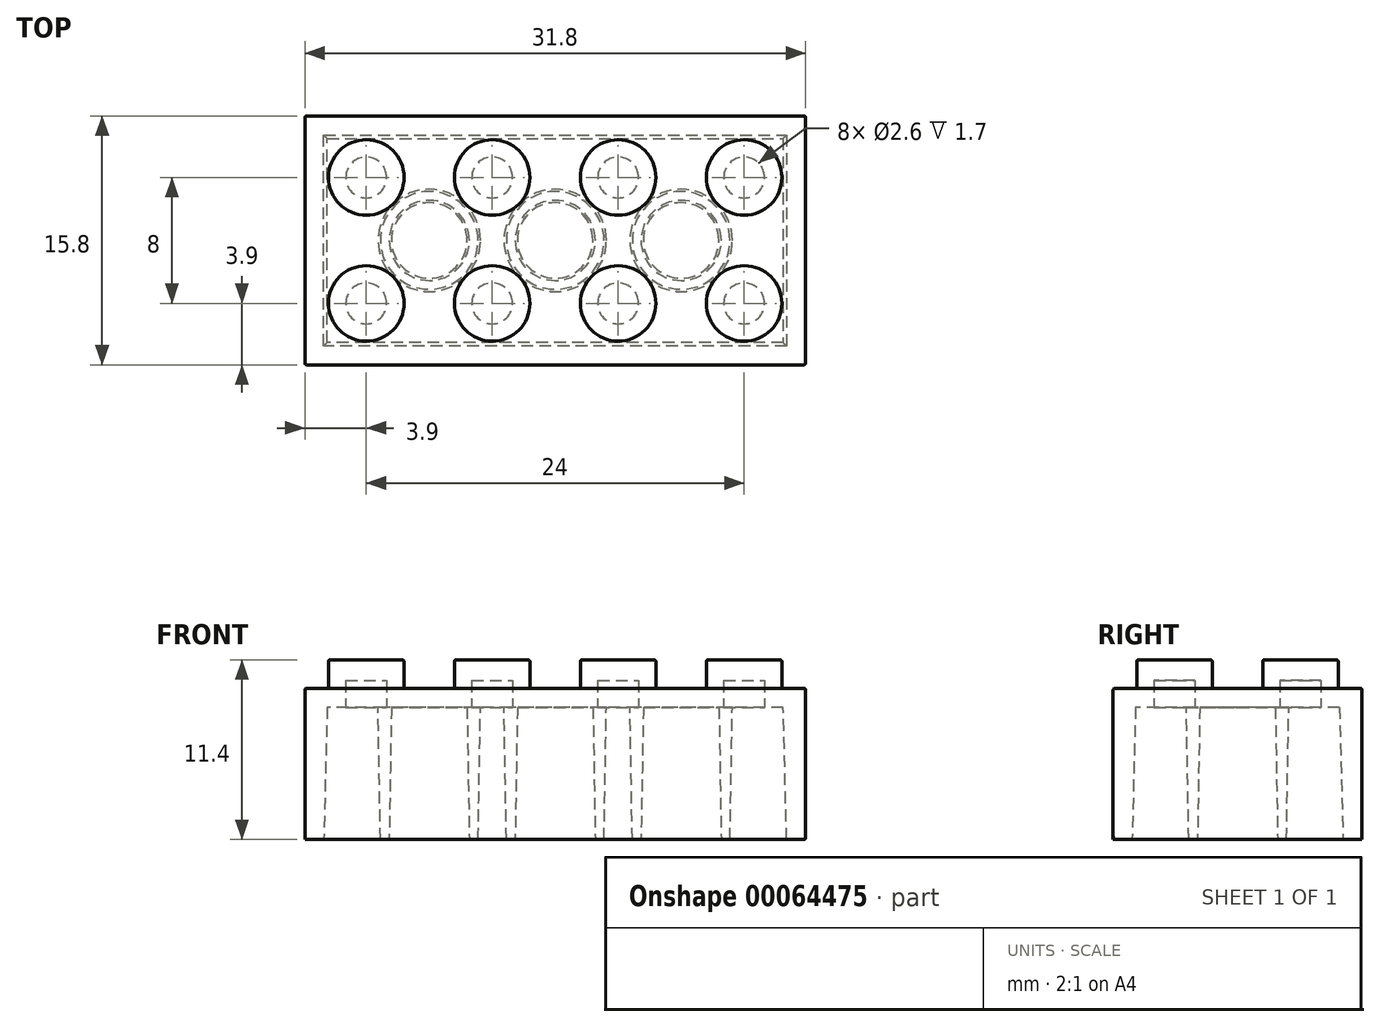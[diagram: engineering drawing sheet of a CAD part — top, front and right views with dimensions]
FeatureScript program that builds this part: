
annotation { "Feature Type Name" : "Feature", "Feature Type Description" : "" }
export const myFeature = defineFeature(function(context is Context, id is Id, definition is map)
    precondition{}
    {
        {
            var Q0;
            Q0=qCreatedBy(makeId("Top.planeOp"),FACE);
            var sketch = newSketch(context, id + "F0", { "sketchPlane" : qUnion([Q0])});
            skLineSegment(sketch, "E0.rect.bottom", {"start": v(15.9, -7.9) * mm, "end": v(-15.9, -7.9) * mm});
            skLineSegment(sketch, "E0.rect.top", {"start": v(15.9, 7.9) * mm, "end": v(-15.9, 7.9) * mm});
            skLineSegment(sketch, "E0.rect.left", {"start": v(15.9, -7.9) * mm, "end": v(15.9, 7.9) * mm});
            skLineSegment(sketch, "E0.rect.right", {"start": v(-15.9, -7.9) * mm, "end": v(-15.9, 7.9) * mm});
            skPoint(sketch, "E0.rect.middle", {"position": v(0, 0) * mm});
            skSolve(sketch);
        }
        {
            var Q0;
            Q0 = qSketchRegion(id + "F0", true);
            extrude(context, id + "F1", {"entities" : qUnion([Q0]), "depth" : 9.6 * mm});
        }
        {
            var Q0;
            Q0=makeQuery(id+"F1.opExtrude","CAP_FACE",FACE,{"disambiguationData":[OSD([sQuery(id+"F0.wireOp",EDGE,"E0.rect.bottom"),sQuery(id+"F0.wireOp",EDGE,"E0.rect.top"),sQuery(id+"F0.wireOp",EDGE,"E0.rect.left"),sQuery(id+"F0.wireOp",EDGE,"E0.rect.right")])],"isStart":false});
            var sketch = newSketch(context, id + "F2", { "sketchPlane" : qUnion([Q0])});
            skCircle(sketch, "E1", {"center": v(-12, 4) * mm, "radius": 2.4 * mm});
            skCircle(sketch, "E2.0.1.0", {"center": v(-12, -4) * mm, "radius": 2.4 * mm});
            skCircle(sketch, "E2.1.0.0", {"center": v(-4, 4) * mm, "radius": 2.4 * mm});
            skCircle(sketch, "E2.1.1.0", {"center": v(-4, -4) * mm, "radius": 2.4 * mm});
            skCircle(sketch, "E2.2.0.0", {"center": v(4, 4) * mm, "radius": 2.4 * mm});
            skCircle(sketch, "E2.2.1.0", {"center": v(4, -4) * mm, "radius": 2.4 * mm});
            skCircle(sketch, "E2.3.0.0", {"center": v(12, 4) * mm, "radius": 2.4 * mm});
            skCircle(sketch, "E2.3.1.0", {"center": v(12, -4) * mm, "radius": 2.4 * mm});
            skLineSegment(sketch, "E2.direction1", {"start": v(-12, 4) * mm, "end": v(-4, 4) * mm, "construction": true});
            skLineSegment(sketch, "E2.direction2", {"start": v(-12, 4) * mm, "end": v(-12, -4) * mm, "construction": true});
            skSolve(sketch);
        }
        {
            var Q0;
            Q0 = qSketchRegion(id + "F2", true);
            extrude(context, id + "F3", {"entities" : qUnion([Q0]), "operationType" : NewBodyOperationType.ADD, "depth" : 1.8 * mm});
        }
        {
            var Q0;
            Q0=makeQuery(id+"F0.imprint","IMPRINT",FACE,{"disambiguationData":[TD([[makeQuery(id+"F0.imprint","IMPRINT",EDGE,{"derivedFrom":sQuery(id+"F0.wireOp",EDGE,"E0.rect.bottom")}),-1.0]])]});
            var sketch = newSketch(context, id + "F4", { "sketchPlane" : qUnion([Q0])});
            skLineSegment(sketch, "E3.0", {"start": v(14.7, -6.7) * mm, "end": v(-14.7, -6.7) * mm});
            skLineSegment(sketch, "E3.1", {"start": v(14.7, -6.7) * mm, "end": v(14.7, 6.7) * mm});
            skLineSegment(sketch, "E3.2", {"start": v(14.7, 6.7) * mm, "end": v(-14.7, 6.7) * mm});
            skLineSegment(sketch, "E3.3", {"start": v(-14.7, -6.7) * mm, "end": v(-14.7, 6.7) * mm});
            skSolve(sketch);
        }
        {
            var Q0;
            Q0=makeQuery(id+"F4.imprint","IMPRINT",FACE,{"disambiguationData":[TD([[makeQuery(id+"F4.imprint","IMPRINT",EDGE,{"derivedFrom":sQuery(id+"F4.wireOp",EDGE,"E3.0")}),-1.0]])]});
            extrude(context, id + "F5", {"entities" : qUnion([Q0]), "operationType" : NewBodyOperationType.REMOVE, "depth" : (9.6 - 1.2) * mm, "hasDraft" : true, "draftAngle" : 1.5 * degree, "draftPullDirection" : true});
        }
        {
            var Q0;
            Q0=makeQuery(id+"F5.boolean.opBoolean","COPY",FACE,{"derivedFrom":makeQuery(id+"F5.opExtrude","CAP_FACE",FACE,{"disambiguationData":[OSD([sQuery(id+"F4.wireOp",EDGE,"E3.0"),sQuery(id+"F4.wireOp",EDGE,"E3.1"),sQuery(id+"F4.wireOp",EDGE,"E3.2"),sQuery(id+"F4.wireOp",EDGE,"E3.3")])],"isStart":false})});
            var sketch = newSketch(context, id + "F6", { "sketchPlane" : qUnion([Q0])});
            skCircle(sketch, "E4.0", {"center": v(-12, -4) * mm, "radius": 2.4 * mm, "construction": true});
            skCircle(sketch, "E5.0", {"center": v(-12, 4) * mm, "radius": 2.4 * mm, "construction": true});
            skCircle(sketch, "E6.0", {"center": v(-4, 4) * mm, "radius": 2.4 * mm, "construction": true});
            skCircle(sketch, "E7.0", {"center": v(-4, -4) * mm, "radius": 2.4 * mm, "construction": true});
            skCircle(sketch, "E8.0", {"center": v(4, -4) * mm, "radius": 2.4 * mm, "construction": true});
            skCircle(sketch, "E9.0", {"center": v(4, 4) * mm, "radius": 2.4 * mm, "construction": true});
            skCircle(sketch, "E10.0", {"center": v(12, 4) * mm, "radius": 2.4 * mm, "construction": true});
            skCircle(sketch, "E11.0", {"center": v(12, -4) * mm, "radius": 2.4 * mm, "construction": true});
            skCircle(sketch, "E12", {"center": v(-12, 4) * mm, "radius": 1.3 * mm});
            skCircle(sketch, "E13", {"center": v(-4, 4) * mm, "radius": 1.3 * mm});
            skCircle(sketch, "E14", {"center": v(4, 4) * mm, "radius": 1.3 * mm});
            skCircle(sketch, "E15", {"center": v(12, 4) * mm, "radius": 1.3 * mm});
            skCircle(sketch, "E16", {"center": v(-12, -4) * mm, "radius": 1.3 * mm});
            skCircle(sketch, "E17", {"center": v(-4, -4) * mm, "radius": 1.3 * mm});
            skCircle(sketch, "E18", {"center": v(4, -4) * mm, "radius": 1.3 * mm});
            skCircle(sketch, "E19", {"center": v(12, -4) * mm, "radius": 1.3 * mm});
            skSolve(sketch);
        }
        {
            var Q0;
            Q0=makeQuery(id+"F6.imprint","IMPRINT",FACE,{"disambiguationData":[TD([[makeQuery(id+"F6.imprint","IMPRINT",EDGE,{"derivedFrom":sQuery(id+"F6.wireOp",EDGE,"E12")}),1.0]])]});
            var Q1;
            Q1=makeQuery(id+"F6.imprint","IMPRINT",FACE,{"disambiguationData":[TD([[makeQuery(id+"F6.imprint","IMPRINT",EDGE,{"derivedFrom":sQuery(id+"F6.wireOp",EDGE,"E13")}),1.0]])]});
            var Q2;
            Q2=makeQuery(id+"F6.imprint","IMPRINT",FACE,{"disambiguationData":[TD([[makeQuery(id+"F6.imprint","IMPRINT",EDGE,{"derivedFrom":sQuery(id+"F6.wireOp",EDGE,"E14")}),1.0]])]});
            var Q3;
            Q3=makeQuery(id+"F6.imprint","IMPRINT",FACE,{"disambiguationData":[TD([[makeQuery(id+"F6.imprint","IMPRINT",EDGE,{"derivedFrom":sQuery(id+"F6.wireOp",EDGE,"E15")}),1.0]])]});
            var Q4;
            Q4=makeQuery(id+"F6.imprint","IMPRINT",FACE,{"disambiguationData":[TD([[makeQuery(id+"F6.imprint","IMPRINT",EDGE,{"derivedFrom":sQuery(id+"F6.wireOp",EDGE,"E16")}),1.0]])]});
            var Q5;
            Q5=makeQuery(id+"F6.imprint","IMPRINT",FACE,{"disambiguationData":[TD([[makeQuery(id+"F6.imprint","IMPRINT",EDGE,{"derivedFrom":sQuery(id+"F6.wireOp",EDGE,"E17")}),1.0]])]});
            var Q6;
            Q6=makeQuery(id+"F6.imprint","IMPRINT",FACE,{"disambiguationData":[TD([[makeQuery(id+"F6.imprint","IMPRINT",EDGE,{"derivedFrom":sQuery(id+"F6.wireOp",EDGE,"E18")}),1.0]])]});
            var Q7;
            Q7=makeQuery(id+"F6.imprint","IMPRINT",FACE,{"disambiguationData":[TD([[makeQuery(id+"F6.imprint","IMPRINT",EDGE,{"derivedFrom":sQuery(id+"F6.wireOp",EDGE,"E19")}),1.0]])]});
            extrude(context, id + "F7", {"entities" : qUnion([Q0, Q1, Q2, Q3, Q4, Q5, Q6, Q7]), "operationType" : NewBodyOperationType.REMOVE, "oppositeDirection" : true, "depth" : 1.7 * mm});
        }
        {
            var Q0;
            Q0=makeQuery(id+"F5.boolean.opBoolean","COPY",FACE,{"derivedFrom":makeQuery(id+"F5.opExtrude","CAP_FACE",FACE,{"disambiguationData":[OSD([sQuery(id+"F4.wireOp",EDGE,"E3.0"),sQuery(id+"F4.wireOp",EDGE,"E3.1"),sQuery(id+"F4.wireOp",EDGE,"E3.2"),sQuery(id+"F4.wireOp",EDGE,"E3.3")])],"isStart":false})});
            var sketch = newSketch(context, id + "F8", { "sketchPlane" : qUnion([Q0])});
            skLineSegment(sketch, "E20.0", {"start": v(-15.9, 7.9) * mm, "end": v(-15.9, -7.9) * mm, "construction": true});
            skCircle(sketch, "E21", {"center": v(0, 0) * mm, "radius": 3.25 * mm});
            skCircle(sketch, "E22", {"center": v(8, 0) * mm, "radius": 3.25 * mm});
            skCircle(sketch, "E23", {"center": v(-8, 0) * mm, "radius": 3.25 * mm});
            skLineSegment(sketch, "E24", {"start": v(-12, 4) * mm, "end": v(-4, -4) * mm, "construction": true});
            skLineSegment(sketch, "E25", {"start": v(4, -4) * mm, "end": v(12, 4) * mm, "construction": true});
            skCircle(sketch, "E26", {"center": v(-8, 0) * mm, "radius": 2.4 * mm});
            skCircle(sketch, "E27", {"center": v(0, 0) * mm, "radius": 2.4 * mm});
            skCircle(sketch, "E28", {"center": v(8, 0) * mm, "radius": 2.4 * mm});
            skSolve(sketch);
        }
        {
            var Q0;
            Q0 = qSketchRegion(id + "F8", true);
            var Q1;
            Q1=makeQuery(id+"F1.opExtrude","CAP_FACE",FACE,{"disambiguationData":[OSD([sQuery(id+"F0.wireOp",EDGE,"E0.rect.bottom"),sQuery(id+"F0.wireOp",EDGE,"E0.rect.top"),sQuery(id+"F0.wireOp",EDGE,"E0.rect.left"),sQuery(id+"F0.wireOp",EDGE,"E0.rect.right")])],"isStart":true});
            extrude(context, id + "F9", {"entities" : qUnion([Q0]), "operationType" : NewBodyOperationType.ADD, "endBound" : BoundingType.UP_TO_SURFACE, "endBoundEntityFace" : qUnion([Q1]), "depth" : 25 * mm, "hasDraft" : true, "draftAngle" : 1 * degree, "draftPullDirection" : true});
        }
        {
            var Q0;
            Q0=makeQuery(id+"F3.opExtrude","CAP_EDGE",EDGE,{"disambiguationData":[OSD([sQuery(id+"F2.wireOp",EDGE,"E2.3.1.0")])],"isStart":false});
            var Q1;
            Q1=makeQuery(id+"F3.opExtrude","CAP_EDGE",EDGE,{"disambiguationData":[OSD([sQuery(id+"F2.wireOp",EDGE,"E2.2.1.0")])],"isStart":false});
            var Q2;
            Q2=makeQuery(id+"F3.opExtrude","CAP_EDGE",EDGE,{"disambiguationData":[OSD([sQuery(id+"F2.wireOp",EDGE,"E2.1.1.0")])],"isStart":false});
            var Q3;
            Q3=makeQuery(id+"F3.opExtrude","CAP_EDGE",EDGE,{"disambiguationData":[OSD([sQuery(id+"F2.wireOp",EDGE,"E2.0.1.0")])],"isStart":false});
            var Q4;
            Q4=makeQuery(id+"F3.opExtrude","CAP_EDGE",EDGE,{"disambiguationData":[OSD([sQuery(id+"F2.wireOp",EDGE,"E1")])],"isStart":false});
            var Q5;
            Q5=makeQuery(id+"F3.opExtrude","CAP_EDGE",EDGE,{"disambiguationData":[OSD([sQuery(id+"F2.wireOp",EDGE,"E2.1.0.0")])],"isStart":false});
            var Q6;
            Q6=makeQuery(id+"F3.opExtrude","CAP_EDGE",EDGE,{"disambiguationData":[OSD([sQuery(id+"F2.wireOp",EDGE,"E2.2.0.0")])],"isStart":false});
            var Q7;
            Q7=makeQuery(id+"F3.opExtrude","CAP_EDGE",EDGE,{"disambiguationData":[OSD([sQuery(id+"F2.wireOp",EDGE,"E2.3.0.0")])],"isStart":false});
            var Q8;
            Q8=makeQuery(id+"F3.opExtrude","CAP_EDGE",EDGE,{"disambiguationData":[OSD([sQuery(id+"F2.wireOp",EDGE,"E1")])],"isStart":true});
            var Q9;
            Q9=makeQuery(id+"F3.opExtrude","CAP_EDGE",EDGE,{"disambiguationData":[OSD([sQuery(id+"F2.wireOp",EDGE,"E2.0.1.0")])],"isStart":true});
            var Q10;
            Q10=makeQuery(id+"F3.opExtrude","CAP_EDGE",EDGE,{"disambiguationData":[OSD([sQuery(id+"F2.wireOp",EDGE,"E2.1.1.0")])],"isStart":true});
            var Q11;
            Q11=makeQuery(id+"F3.opExtrude","CAP_EDGE",EDGE,{"disambiguationData":[OSD([sQuery(id+"F2.wireOp",EDGE,"E2.1.0.0")])],"isStart":true});
            var Q12;
            Q12=makeQuery(id+"F3.opExtrude","CAP_EDGE",EDGE,{"disambiguationData":[OSD([sQuery(id+"F2.wireOp",EDGE,"E2.2.0.0")])],"isStart":true});
            var Q13;
            Q13=makeQuery(id+"F3.opExtrude","CAP_EDGE",EDGE,{"disambiguationData":[OSD([sQuery(id+"F2.wireOp",EDGE,"E2.2.1.0")])],"isStart":true});
            var Q14;
            Q14=makeQuery(id+"F3.opExtrude","CAP_EDGE",EDGE,{"disambiguationData":[OSD([sQuery(id+"F2.wireOp",EDGE,"E2.3.0.0")])],"isStart":true});
            var Q15;
            Q15=makeQuery(id+"F3.opExtrude","CAP_EDGE",EDGE,{"disambiguationData":[OSD([sQuery(id+"F2.wireOp",EDGE,"E2.3.1.0")])],"isStart":true});
            var Q16;
            Q16=makeQuery(id+"F1.opExtrude","CAP_EDGE",EDGE,{"disambiguationData":[OSD([sQuery(id+"F0.wireOp",EDGE,"E0.rect.left")])],"isStart":false});
            var Q17;
            Q17=makeQuery(id+"F1.opExtrude","SWEPT_FACE",FACE,{"disambiguationData":[OSD([sQuery(id+"F0.wireOp",EDGE,"E0.rect.left")])]});
            var Q18;
            Q18=makeQuery(id+"F1.opExtrude","CAP_EDGE",EDGE,{"disambiguationData":[OSD([sQuery(id+"F0.wireOp",EDGE,"E0.rect.top")])],"isStart":false});
            var Q19;
            Q19=makeQuery(id+"F1.opExtrude","SWEPT_EDGE",EDGE,{"disambiguationData":[OSD([sQuery(id+"F0.wireOp",EDGE,"E0.rect.top"),sQuery(id+"F0.wireOp",EDGE,"E0.rect.left")])]});
            var Q20;
            Q20=makeQuery(id+"F1.opExtrude","SWEPT_EDGE",EDGE,{"disambiguationData":[OSD([sQuery(id+"F0.wireOp",EDGE,"E0.rect.bottom"),sQuery(id+"F0.wireOp",EDGE,"E0.rect.left")])]});
            var Q21;
            Q21=makeQuery(id+"F1.opExtrude","SWEPT_EDGE",EDGE,{"disambiguationData":[OSD([sQuery(id+"F0.wireOp",EDGE,"E0.rect.top"),sQuery(id+"F0.wireOp",EDGE,"E0.rect.right")])]});
            var Q22;
            Q22=makeQuery(id+"F1.opExtrude","SWEPT_EDGE",EDGE,{"disambiguationData":[OSD([sQuery(id+"F0.wireOp",EDGE,"E0.rect.bottom"),sQuery(id+"F0.wireOp",EDGE,"E0.rect.right")])]});
            var Q23;
            Q23=makeQuery(id+"F1.opExtrude","CAP_EDGE",EDGE,{"disambiguationData":[OSD([sQuery(id+"F0.wireOp",EDGE,"E0.rect.right")])],"isStart":false});
            var Q24;
            Q24=makeQuery(id+"F1.opExtrude","CAP_EDGE",EDGE,{"disambiguationData":[OSD([sQuery(id+"F0.wireOp",EDGE,"E0.rect.bottom")])],"isStart":false});
            fillet(context, id + "F10", {"entities" : qUnion([Q0, Q1, Q2, Q3, Q4, Q5, Q6, Q7, Q8, Q9, Q10, Q11, Q12, Q13, Q14, Q15, Q16, Q17, Q18, Q19, Q20, Q21, Q22, Q23, Q24]), "radius" : .1 * mm, "tangentPropagation" : true, "allowEdgeOverflow" : false});
        }
    });
